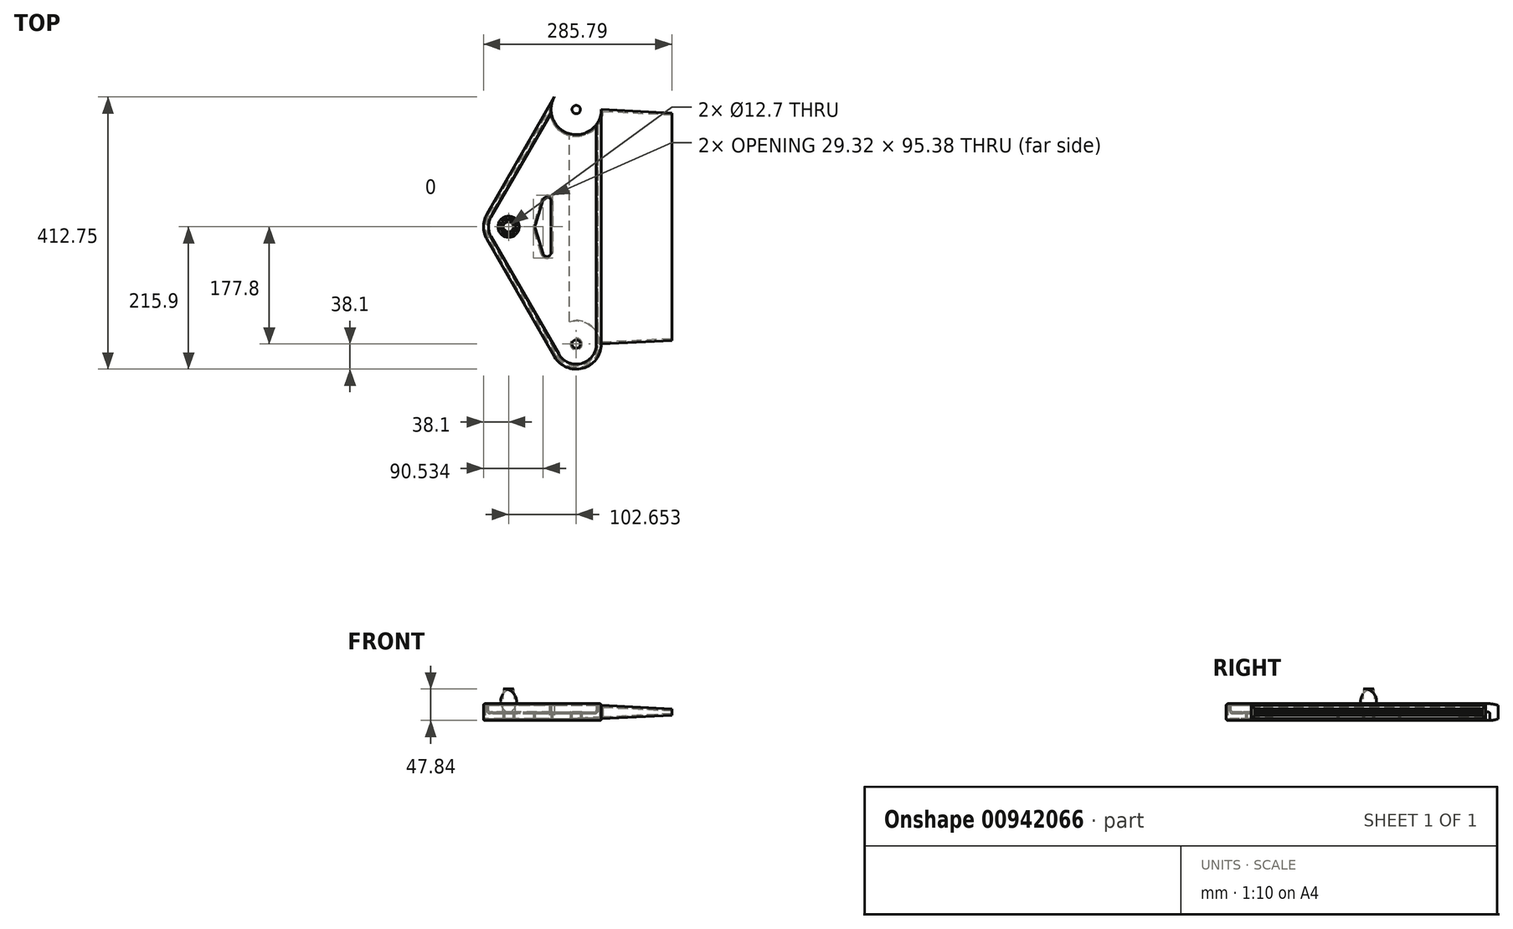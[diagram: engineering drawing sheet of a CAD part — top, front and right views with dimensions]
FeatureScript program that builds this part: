
annotation { "Feature Type Name" : "Feature", "Feature Type Description" : "" }
export const myFeature = defineFeature(function(context is Context, id is Id, definition is map)
    precondition{}
    {
        {
            var Q0;
            Q0=qCreatedBy(makeId("Top.planeOp"),FACE);
            var sketch = newSketch(context, id + "F0", { "sketchPlane" : qUnion([Q0])});
            skLineSegment(sketch, "E0", {"start": v(0, 0) * mm, "end": v(102.65, 0) * mm, "construction": true});
            skLineSegment(sketch, "E1", {"start": v(0, 0) * mm, "end": v(102.65, 177.8) * mm, "construction": true});
            skLineSegment(sketch, "E2.MirrorCS", {"start": v(0, 0) * mm, "end": v(102.65, -177.8) * mm, "construction": true});
            skLineSegment(sketch, "E3", {"start": v(102.65, 177.8) * mm, "end": v(102.65, -177.8) * mm, "construction": true});
            skCircle(sketch, "E4", {"center": v(0, 0) * mm, "radius": 38.1 * mm});
            skCircle(sketch, "E5", {"center": v(0, 0) * mm, "radius": 6.35 * mm});
            skLineSegment(sketch, "E6", {"start": v(51.33, 88.9) * mm, "end": v(-111.46, 182.88) * mm, "construction": true});
            skCircle(sketch, "E7.MirrorC", {"center": v(102.65, 177.8) * mm, "radius": 38.1 * mm});
            skCircle(sketch, "E8.MirrorC", {"center": v(102.65, 177.8) * mm, "radius": 6.35 * mm});
            skCircle(sketch, "E9.MirrorC", {"center": v(102.65, -177.8) * mm, "radius": 38.1 * mm});
            skCircle(sketch, "E10.MirrorC", {"center": v(102.65, -177.8) * mm, "radius": 6.35 * mm});
            skLineSegment(sketch, "E11", {"start": v(-33, 19.05) * mm, "end": v(69.66, 196.85) * mm});
            skLineSegment(sketch, "E12", {"start": v(-33, -19.05) * mm, "end": v(69.66, -196.85) * mm});
            skLineSegment(sketch, "E13", {"start": v(140.75, 177.8) * mm, "end": v(140.75, -177.8) * mm});
            skLineSegment(sketch, "E14", {"start": v(40.8, -3.3) * mm, "end": v(52.12, -40.73) * mm});
            skLineSegment(sketch, "E15.MirrorCS", {"start": v(40.8, 3.3) * mm, "end": v(52.12, 40.73) * mm});
            skLineSegment(sketch, "E16.MirrorCS", {"start": v(64.55, 38.9) * mm, "end": v(64.55, -38.9) * mm});
            skPoint(sketch, "E17.orphan", {"position": v(64.55, 177.8) * mm});
            skPoint(sketch, "E18.orphan", {"position": v(83.6, 144.8) * mm});
            skPoint(sketch, "E19.orphan", {"position": v(36.47, -11.03) * mm});
            skPoint(sketch, "E20.orphan", {"position": v(36.47, 11.03) * mm});
            skPoint(sketch, "E21.trimOffspring.end.orphan", {"position": v(64.55, -177.8) * mm});
            skPoint(sketch, "E22.orphan", {"position": v(83.6, -144.8) * mm});
            skPoint(sketch, "E23.visualSharp", {"position": v(64.55, 81.82) * mm});
            skArc(sketch, "E23.filletArc", {"start": v(64.55, 38.9) * mm, "mid": v(59.13, 45.18) * mm, "end": v(52.12, 40.73) * mm});
            skPoint(sketch, "E24.visualSharp", {"position": v(39.8, 0) * mm});
            skArc(sketch, "E24.filletArc", {"start": v(40.8, 3.3) * mm, "mid": v(40.32, 0) * mm, "end": v(40.8, -3.3) * mm});
            skPoint(sketch, "E25.visualSharp", {"position": v(64.55, -81.82) * mm});
            skArc(sketch, "E25.filletArc", {"start": v(52.12, -40.73) * mm, "mid": v(59.13, -45.18) * mm, "end": v(64.55, -38.9) * mm});
            skSolve(sketch);
        }
        {
            var Q0;
            {var subQ2=sQuery(id+"F0.wireOp",EDGE,"E11");Q0=makeQuery(id+"F0.imprint","IMPRINT",FACE,{"disambiguationData":[TD([[makeQuery(id+"F0.imprint","IMPRINT",EDGE,{"derivedFrom":subQ2}),-1.0]])]});}
            var Q1;
            Q1=makeQuery(id+"F0.imprint","IMPRINT",FACE,{"disambiguationData":[TD([[makeQuery(id+"F0.imprint","IMPRINT",EDGE,{"derivedFrom":sQuery(id+"F0.wireOp",EDGE,"E10.MirrorC")}),-1.0]])]});
            var Q2;
            Q2=makeQuery(id+"F0.imprint","IMPRINT",FACE,{"disambiguationData":[TD([[makeQuery(id+"F0.imprint","IMPRINT",EDGE,{"derivedFrom":sQuery(id+"F0.wireOp",EDGE,"E5")}),-1.0]])]});
            var Q3;
            Q3=makeQuery(id+"F0.imprint","IMPRINT",FACE,{"disambiguationData":[TD([[makeQuery(id+"F0.imprint","IMPRINT",EDGE,{"derivedFrom":sQuery(id+"F0.wireOp",EDGE,"E8.MirrorC")}),1.0]])]});
            extrude(context, id + "F1", {"entities" : qUnion([Q0, Q1, Q2, Q3]), "depth" : 25.4 * mm, "offsetDistance" : 25.4 * mm});
        }
        {
            var Q0;
            Q0=makeQuery(id+"F1.opExtrude","CAP_FACE",FACE,{"disambiguationData":[OSD([sQuery(id+"F0.wireOp",EDGE,"E4"),sQuery(id+"F0.wireOp",EDGE,"E5"),sQuery(id+"F0.wireOp",EDGE,"E7.MirrorC"),sQuery(id+"F0.wireOp",EDGE,"E8.MirrorC"),sQuery(id+"F0.wireOp",EDGE,"E9.MirrorC"),sQuery(id+"F0.wireOp",EDGE,"E10.MirrorC"),sQuery(id+"F0.wireOp",EDGE,"E11"),sQuery(id+"F0.wireOp",EDGE,"E12"),sQuery(id+"F0.wireOp",EDGE,"E13"),sQuery(id+"F0.wireOp",EDGE,"E14"),sQuery(id+"F0.wireOp",EDGE,"E15.MirrorCS"),sQuery(id+"F0.wireOp",EDGE,"E16.MirrorCS"),sQuery(id+"F0.wireOp",EDGE,"E23.filletArc"),sQuery(id+"F0.wireOp",EDGE,"E24.filletArc"),sQuery(id+"F0.wireOp",EDGE,"E25.filletArc")])],"isStart":false});
            var sketch = newSketch(context, id + "F2", { "sketchPlane" : qUnion([Q0])});
            skArc(sketch, "E26.0", {"start": v(76.26, -193.04) * mm, "mid": v(110.54, -207.24) * mm, "end": v(133.13, -177.8) * mm});
            skArc(sketch, "E26.1", {"start": v(133.13, 177.8) * mm, "mid": v(110.54, 207.24) * mm, "end": v(76.26, 193.04) * mm});
            skLineSegment(sketch, "E26.2", {"start": v(76.26, 193.04) * mm, "end": v(-26.4, 15.24) * mm});
            skLineSegment(sketch, "E26.3", {"start": v(133.13, -177.8) * mm, "end": v(133.13, 177.8) * mm});
            skArc(sketch, "E26.4", {"start": v(-26.4, 15.24) * mm, "mid": v(-30.48, 0) * mm, "end": v(-26.4, -15.24) * mm});
            skLineSegment(sketch, "E26.5", {"start": v(-26.4, -15.24) * mm, "end": v(76.26, -193.04) * mm});
            skSolve(sketch);
        }
        {
            var Q0;
            Q0 = qSketchRegion(id + "F2", true);
            extrude(context, id + "F3", {"entities" : qUnion([Q0]), "operationType" : NewBodyOperationType.REMOVE, "oppositeDirection" : true, "depth" : 12.7 * mm, "offsetDistance" : 25.4 * mm});
        }
        {
            var Q0;
            Q0=makeQuery(id+"F3.boolean.opBoolean","COPY",EDGE,{"derivedFrom":makeQuery(id+"F3.opExtrude","CAP_EDGE",EDGE,{"disambiguationData":[OSD([sQuery(id+"F2.wireOp",EDGE,"E26.2")])],"isStart":false})});
            var Q1;
            Q1=makeQuery(id+"F3.boolean.opBoolean","INTERSECT",EDGE,{"derivedFrom":[makeQuery(id+"F1.opExtrude","SWEPT_FACE",FACE,{"disambiguationData":[OSD([sQuery(id+"F0.wireOp",EDGE,"E15.MirrorCS")])]}),makeQuery(id+"F3.opExtrude","CAP_FACE",FACE,{"disambiguationData":[OSD([sQuery(id+"F2.wireOp",EDGE,"E26.0"),sQuery(id+"F2.wireOp",EDGE,"E26.1"),sQuery(id+"F2.wireOp",EDGE,"E26.2"),sQuery(id+"F2.wireOp",EDGE,"E26.3"),sQuery(id+"F2.wireOp",EDGE,"E26.4"),sQuery(id+"F2.wireOp",EDGE,"E26.5")])],"isStart":false})]});
            var Q2;
            Q2=makeQuery(id+"F3.boolean.opBoolean","COPY",EDGE,{"derivedFrom":makeQuery(id+"F3.opExtrude","CAP_EDGE",EDGE,{"disambiguationData":[OSD([sQuery(id+"F2.wireOp",EDGE,"E26.2")])],"isStart":true})});
            var Q3;
            Q3=makeQuery(id+"F1.opExtrude","CAP_EDGE",EDGE,{"disambiguationData":[OSD([sQuery(id+"F0.wireOp",EDGE,"E11")])],"isStart":false});
            var Q4;
            Q4=makeQuery(id+"F1.opExtrude","CAP_EDGE",EDGE,{"disambiguationData":[OSD([sQuery(id+"F0.wireOp",EDGE,"E4")])],"isStart":false});
            var Q5;
            Q5=makeQuery(id+"F3.boolean.opBoolean","INTERSECT",EDGE,{"derivedFrom":[makeQuery(id+"F1.opExtrude","SWEPT_FACE",FACE,{"disambiguationData":[OSD([sQuery(id+"F0.wireOp",EDGE,"E5")])]}),makeQuery(id+"F3.opExtrude","CAP_FACE",FACE,{"disambiguationData":[OSD([sQuery(id+"F2.wireOp",EDGE,"E26.0"),sQuery(id+"F2.wireOp",EDGE,"E26.1"),sQuery(id+"F2.wireOp",EDGE,"E26.2"),sQuery(id+"F2.wireOp",EDGE,"E26.3"),sQuery(id+"F2.wireOp",EDGE,"E26.4"),sQuery(id+"F2.wireOp",EDGE,"E26.5")])],"isStart":false})]});
            var Q6;
            Q6=makeQuery(id+"F3.boolean.opBoolean","INTERSECT",EDGE,{"derivedFrom":[makeQuery(id+"F1.opExtrude","SWEPT_FACE",FACE,{"disambiguationData":[OSD([sQuery(id+"F0.wireOp",EDGE,"E8.MirrorC")])]}),makeQuery(id+"F3.opExtrude","CAP_FACE",FACE,{"disambiguationData":[OSD([sQuery(id+"F2.wireOp",EDGE,"E26.0"),sQuery(id+"F2.wireOp",EDGE,"E26.1"),sQuery(id+"F2.wireOp",EDGE,"E26.2"),sQuery(id+"F2.wireOp",EDGE,"E26.3"),sQuery(id+"F2.wireOp",EDGE,"E26.4"),sQuery(id+"F2.wireOp",EDGE,"E26.5")])],"isStart":false})]});
            var Q7;
            Q7=makeQuery(id+"F3.boolean.opBoolean","INTERSECT",EDGE,{"derivedFrom":[makeQuery(id+"F1.opExtrude","SWEPT_FACE",FACE,{"disambiguationData":[OSD([sQuery(id+"F0.wireOp",EDGE,"E10.MirrorC")])]}),makeQuery(id+"F3.opExtrude","CAP_FACE",FACE,{"disambiguationData":[OSD([sQuery(id+"F2.wireOp",EDGE,"E26.0"),sQuery(id+"F2.wireOp",EDGE,"E26.1"),sQuery(id+"F2.wireOp",EDGE,"E26.2"),sQuery(id+"F2.wireOp",EDGE,"E26.3"),sQuery(id+"F2.wireOp",EDGE,"E26.4"),sQuery(id+"F2.wireOp",EDGE,"E26.5")])],"isStart":false})]});
            var Q8;
            Q8=makeQuery(id+"F1.opExtrude","CAP_EDGE",EDGE,{"disambiguationData":[OSD([sQuery(id+"F0.wireOp",EDGE,"E16.MirrorCS")])],"isStart":true});
            var Q9;
            Q9=makeQuery(id+"F1.opExtrude","CAP_EDGE",EDGE,{"disambiguationData":[OSD([sQuery(id+"F0.wireOp",EDGE,"E13")])],"isStart":true});
            var Q10;
            Q10=makeQuery(id+"F1.opExtrude","CAP_EDGE",EDGE,{"disambiguationData":[OSD([sQuery(id+"F0.wireOp",EDGE,"E5")])],"isStart":true});
            var Q11;
            Q11=makeQuery(id+"F1.opExtrude","CAP_EDGE",EDGE,{"disambiguationData":[OSD([sQuery(id+"F0.wireOp",EDGE,"E8.MirrorC")])],"isStart":true});
            var Q12;
            Q12=makeQuery(id+"F1.opExtrude","CAP_EDGE",EDGE,{"disambiguationData":[OSD([sQuery(id+"F0.wireOp",EDGE,"E10.MirrorC")])],"isStart":true});
            fillet(context, id + "F4", {"entities" : qUnion([Q0, Q1, Q2, Q3, Q4, Q5, Q6, Q7, Q8, Q9, Q10, Q11, Q12]), "radius" : 2.54 * mm, "tangentPropagation" : true, "allowEdgeOverflow" : false});
        }
        {
            var Q0;
            Q0=makeQuery(id+"F1.opExtrude","SWEPT_FACE",FACE,{"disambiguationData":[OSD([sQuery(id+"F0.wireOp",EDGE,"E13")])]});
            extrude(context, id + "F5", {"entities" : qUnion([Q0]), "operationType" : NewBodyOperationType.ADD, "depth" : 106.93 * mm, "offsetDistance" : 25.4 * mm, "hasDraft" : true, "draftAngle" : 3 * degree, "draftPullDirection" : true});
        }
        {
            var Q0;
            Q0=makeQuery(id+"F5.opExtrude","CAP_FACE",FACE,{"disambiguationData":[OSD([sQuery(id+"F0.wireOp",EDGE,"E13")])],"isStart":false});
            shell(context, id + "F6", {"entities" : qUnion([Q0]), "thickness" : 2.54 * mm});
        }
        {
            var Q0;
            Q0=qCreatedBy(makeId("Front.planeOp"),FACE);
            var sketch = newSketch(context, id + "F7", { "sketchPlane" : qUnion([Q0])});
            skArc(sketch, "E27", {"start": v(-8.12, 47.78) * mm, "mid": v(-25.46, 29.75) * mm, "end": v(-9.57, 10.43) * mm});
            skLineSegment(sketch, "E28", {"start": v(-8.12, 47.78) * mm, "end": v(-9.57, 10.43) * mm});
            skSolve(sketch);
        }
        {
            var Q0;
            Q0=makeQuery(id+"F7.imprint","IMPRINT",FACE,{"disambiguationData":[TD([[makeQuery(id+"F7.imprint","IMPRINT",EDGE,{"derivedFrom":sQuery(id+"F7.wireOp",EDGE,"E27")}),1.0]])]});
            var Q1;
            {var subQ0=makeQuery(id+"F3.opExtrude","CAP_FACE",FACE,{"disambiguationData":[OSD([sQuery(id+"F2.wireOp",EDGE,"E26.0"),sQuery(id+"F2.wireOp",EDGE,"E26.1"),sQuery(id+"F2.wireOp",EDGE,"E26.2"),sQuery(id+"F2.wireOp",EDGE,"E26.3"),sQuery(id+"F2.wireOp",EDGE,"E26.4"),sQuery(id+"F2.wireOp",EDGE,"E26.5")])],"isStart":false});Q1=makeQuery(id+"F4.opFillet","BLEND_EDGE",EDGE,{"blendedFrom":[makeQuery(id+"F3.boolean.opBoolean","INTERSECT",EDGE,{"derivedFrom":[makeQuery(id+"F1.opExtrude","SWEPT_FACE",FACE,{"disambiguationData":[OSD([sQuery(id+"F0.wireOp",EDGE,"E5")])]}),subQ0]}),makeQuery(id+"F3.boolean.opBoolean","COPY",FACE,{"derivedFrom":subQ0})],"blendedInto":[makeQuery(id+"F3.boolean.opBoolean","COPY",FACE,{"derivedFrom":subQ0})]});}
            revolve(context, id + "F8", {"operationType" : NewBodyOperationType.ADD, "surfaceOperationType" : NewSurfaceOperationType.NEW, "entities" : qUnion([Q0]), "axis" : qUnion([Q1]), "revolveType" : RevolveType.FULL});
        }
    });
